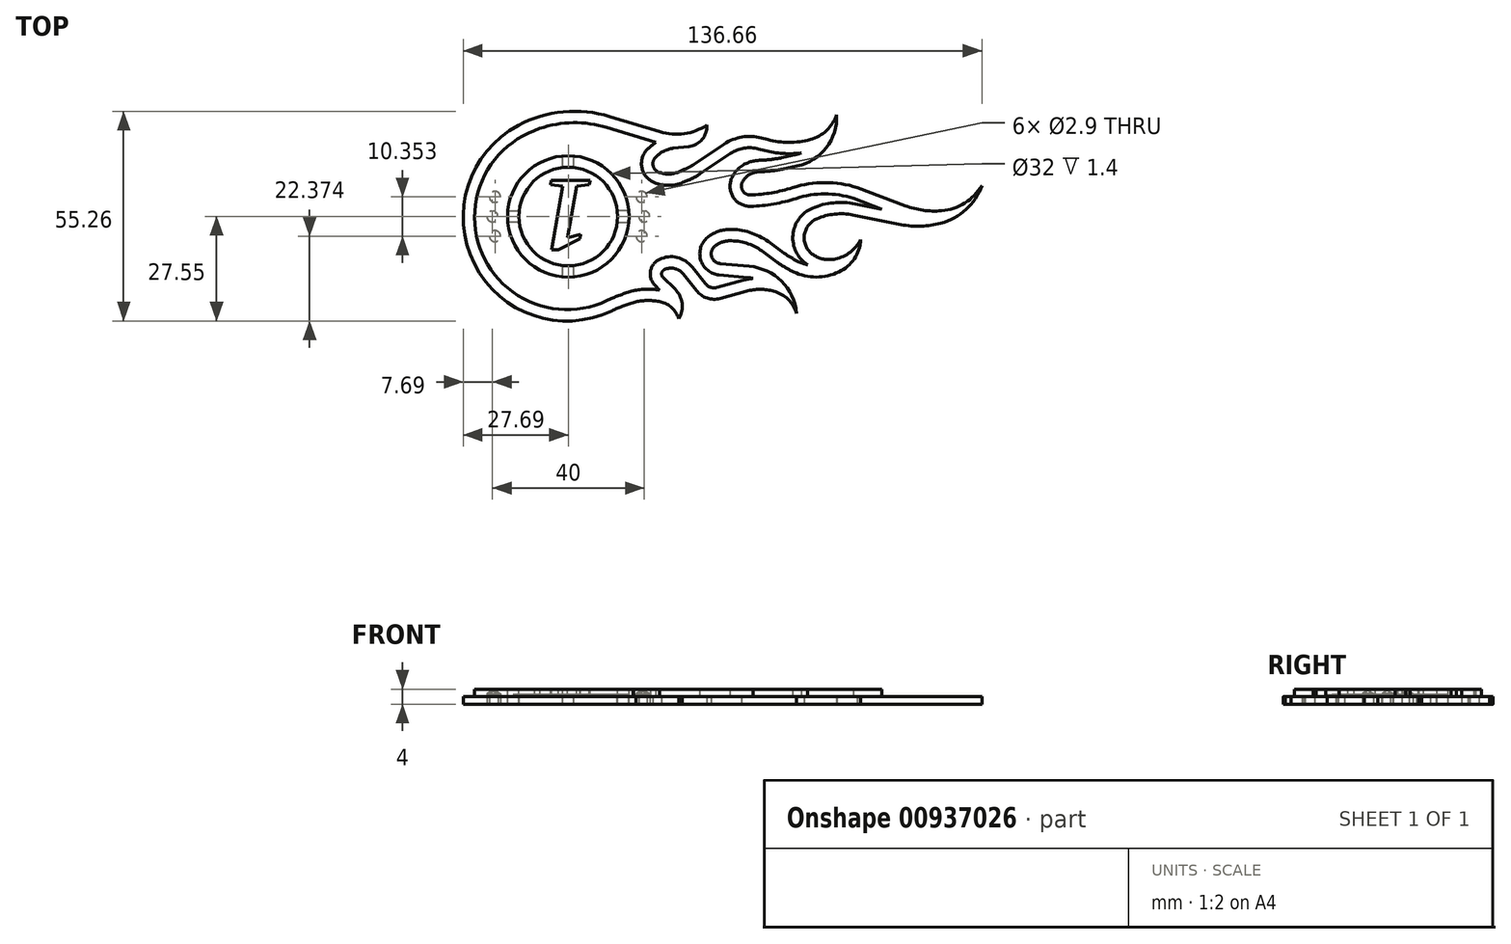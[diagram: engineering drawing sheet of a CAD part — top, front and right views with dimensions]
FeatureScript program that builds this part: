
annotation { "Feature Type Name" : "Feature", "Feature Type Description" : "" }
export const myFeature = defineFeature(function(context is Context, id is Id, definition is map)
    precondition{}
    {
        {
            var Q0;
            Q0=qCreatedBy(makeId("Top.planeOp"),FACE);
            var sketch = newSketch(context, id + "F0", { "sketchPlane" : qUnion([Q0])});
            skArc(sketch, "E0", {"start": v(-15.8, 20.8) * mm, "mid": v(-9.44, 20.3) * mm, "end": v(-3.49, 22.58) * mm});
            skLineSegment(sketch, "E1", {"start": v(-29, 24.82) * mm, "end": v(-15.8, 20.8) * mm});
            skArc(sketch, "E2", {"start": v(-53.14, 22.5) * mm, "mid": v(-64.76, -14.01) * mm, "end": v(-28.48, -26.36) * mm});
            skArc(sketch, "E3", {"start": v(-29, 24.82) * mm, "mid": v(-41.3, 26.06) * mm, "end": v(-53.14, 22.5) * mm});
            skArc(sketch, "E4", {"start": v(-8.25, 16.94) * mm, "mid": v(-4.75, 18.81) * mm, "end": v(-3.49, 22.58) * mm});
            skArc(sketch, "E5", {"start": v(-10.87, -28.44) * mm, "mid": v(-12.7, -25.58) * mm, "end": v(-15.7, -24) * mm});
            skArc(sketch, "E6", {"start": v(-15.7, -24) * mm, "mid": v(-18.94, -23.64) * mm, "end": v(-22.18, -24) * mm});
            skArc(sketch, "E7", {"start": v(-22.18, -24) * mm, "mid": v(-25.39, -25.04) * mm, "end": v(-28.48, -26.36) * mm});
            skArc(sketch, "E8", {"start": v(-10.87, -28.44) * mm, "mid": v(-10.04, -24.35) * mm, "end": v(-11.9, -20.62) * mm});
            skArc(sketch, "E9", {"start": v(-14.69, -15.51) * mm, "mid": v(-15.4, -16.45) * mm, "end": v(-15.02, -17.57) * mm});
            skLineSegment(sketch, "E10", {"start": v(-11.9, -20.62) * mm, "end": v(-15.02, -17.57) * mm});
            skArc(sketch, "E11", {"start": v(-9.7, -16.65) * mm, "mid": v(-12, -15.2) * mm, "end": v(-14.69, -15.51) * mm});
            skLineSegment(sketch, "E12", {"start": v(-9.7, -16.65) * mm, "end": v(-6.22, -21.05) * mm});
            skArc(sketch, "E13", {"start": v(-6.22, -21.05) * mm, "mid": v(-3.42, -23) * mm, "end": v(0, -23.09) * mm});
            skLineSegment(sketch, "E14", {"start": v(-8.25, 16.94) * mm, "end": v(-12.34, 16.47) * mm});
            skArc(sketch, "E15", {"start": v(-12.34, 16.47) * mm, "mid": v(-14.96, 15.66) * mm, "end": v(-17.12, 13.97) * mm});
            skArc(sketch, "E16", {"start": v(-17.12, 13.97) * mm, "mid": v(-17.66, 11.88) * mm, "end": v(-16.27, 10.22) * mm});
            skArc(sketch, "E17", {"start": v(-16.27, 10.22) * mm, "mid": v(-13.63, 9.69) * mm, "end": v(-10.98, 10.22) * mm});
            skLineSegment(sketch, "E18", {"start": v(-10.98, 10.22) * mm, "end": v(-9.42, 10.88) * mm});
            skLineSegment(sketch, "E19", {"start": v(1.1, 17.58) * mm, "end": v(-6.91, 12.23) * mm});
            skArc(sketch, "E20.filletArc", {"start": v(-9.42, 10.88) * mm, "mid": v(-8.13, 11.5) * mm, "end": v(-6.91, 12.23) * mm});
            skArc(sketch, "E21", {"start": v(10.9, 19.2) * mm, "mid": v(5.82, 19.45) * mm, "end": v(1.1, 17.58) * mm});
            skLineSegment(sketch, "E22", {"start": v(10.9, 19.2) * mm, "end": v(12.5, 18.78) * mm});
            skArc(sketch, "E23", {"start": v(12.5, 18.78) * mm, "mid": v(18.13, 18.04) * mm, "end": v(23.76, 18.78) * mm});
            skArc(sketch, "E24", {"start": v(23.76, 18.78) * mm, "mid": v(28.06, 21.17) * mm, "end": v(30.72, 25.31) * mm});
            skArc(sketch, "E25", {"start": v(20.3, 11.8) * mm, "mid": v(27.98, 16.65) * mm, "end": v(30.72, 25.31) * mm});
            skLineSegment(sketch, "E26", {"start": v(20.3, 11.8) * mm, "end": v(16.86, 11.06) * mm});
            skArc(sketch, "E27", {"start": v(10.82, 10.32) * mm, "mid": v(13.86, 10.55) * mm, "end": v(16.86, 11.06) * mm});
            skArc(sketch, "E28", {"start": v(10.82, 10.32) * mm, "mid": v(9.84, 10.23) * mm, "end": v(8.87, 10.03) * mm});
            skArc(sketch, "E29", {"start": v(8.87, 10.03) * mm, "mid": v(7.03, 9.04) * mm, "end": v(5.8, 7.34) * mm});
            skArc(sketch, "E30", {"start": v(5.8, 7.34) * mm, "mid": v(6.02, 5.16) * mm, "end": v(7.97, 4.17) * mm});
            skArc(sketch, "E31", {"start": v(19.12, 6.1) * mm, "mid": v(13.61, 4.74) * mm, "end": v(7.97, 4.17) * mm});
            skArc(sketch, "E32", {"start": v(36.14, 6.1) * mm, "mid": v(27.63, 7.44) * mm, "end": v(19.12, 6.1) * mm});
            skLineSegment(sketch, "E33", {"start": v(0, -23.09) * mm, "end": v(6.9, -21.19) * mm});
            skArc(sketch, "E34", {"start": v(14.19, -21.19) * mm, "mid": v(10.54, -20.7) * mm, "end": v(6.9, -21.19) * mm});
            skArc(sketch, "E35", {"start": v(20.17, -27.02) * mm, "mid": v(17.93, -23.33) * mm, "end": v(14.19, -21.19) * mm});
            skArc(sketch, "E36", {"start": v(20.17, -27.02) * mm, "mid": v(16.15, -18.57) * mm, "end": v(7.68, -14.62) * mm});
            skLineSegment(sketch, "E37", {"start": v(7.68, -14.62) * mm, "end": v(0, -13.91) * mm});
            skArc(sketch, "E38", {"start": v(-1.39, -9.32) * mm, "mid": v(-2.24, -12.08) * mm, "end": v(0, -13.91) * mm});
            skArc(sketch, "E39", {"start": v(2.46, -7.92) * mm, "mid": v(0.42, -8.3) * mm, "end": v(-1.39, -9.32) * mm});
            skArc(sketch, "E40", {"start": v(10.98, -10.59) * mm, "mid": v(6.94, -8.56) * mm, "end": v(2.46, -7.92) * mm});
            skLineSegment(sketch, "E41", {"start": v(10.98, -10.59) * mm, "end": v(15.06, -13.54) * mm});
            skArc(sketch, "E42", {"start": v(15.06, -13.54) * mm, "mid": v(17.16, -14.93) * mm, "end": v(19.37, -16.1) * mm});
            skArc(sketch, "E43", {"start": v(19.37, -16.1) * mm, "mid": v(25.34, -17.46) * mm, "end": v(31.3, -16.1) * mm});
            skArc(sketch, "E44", {"start": v(31.3, -16.1) * mm, "mid": v(35.34, -12.64) * mm, "end": v(37.05, -7.6) * mm});
            skArc(sketch, "E45", {"start": v(30.4, -12.7) * mm, "mid": v(34.29, -10.88) * mm, "end": v(37.05, -7.6) * mm});
            skArc(sketch, "E46", {"start": v(24.84, -11.81) * mm, "mid": v(27.53, -12.78) * mm, "end": v(30.4, -12.7) * mm});
            skArc(sketch, "E47", {"start": v(25.48, -2.1) * mm, "mid": v(22.17, -6.76) * mm, "end": v(24.84, -11.81) * mm});
            skArc(sketch, "E48", {"start": v(35.02, -1.1) * mm, "mid": v(30.17, -0.88) * mm, "end": v(25.48, -2.1) * mm});
            skLineSegment(sketch, "E49", {"start": v(35.02, -1.1) * mm, "end": v(47.7, -3.63) * mm});
            skArc(sketch, "E50", {"start": v(47.7, -3.63) * mm, "mid": v(52.94, -4.06) * mm, "end": v(58.13, -3.3) * mm});
            skArc(sketch, "E51", {"start": v(58.13, -3.3) * mm, "mid": v(64.79, 0.34) * mm, "end": v(68.97, 6.67) * mm});
            skArc(sketch, "E52", {"start": v(58.36, 0) * mm, "mid": v(64.48, 2.05) * mm, "end": v(68.97, 6.67) * mm});
            skArc(sketch, "E53", {"start": v(48.76, 1.34) * mm, "mid": v(53.49, 0.13) * mm, "end": v(58.36, 0) * mm});
            skLineSegment(sketch, "E54", {"start": v(36.14, 6.1) * mm, "end": v(48.76, 1.34) * mm});
            skArc(sketch, "E55.0", {"start": v(-12.68, 19.45) * mm, "mid": v(-12.7, 19.44) * mm, "end": v(-12.72, 19.44) * mm});
            skLineSegment(sketch, "E56", {"start": v(-16.92, 18) * mm, "end": v(-16.92, 18) * mm});
            skLineSegment(sketch, "E57", {"start": v(-19.37, 15.96) * mm, "end": v(-19.34, 15.99) * mm});
            skSolve(sketch);
        }
        {
            var Q0;
            Q0=qSketchRegion(id+"F0",true);
            extrude(context, id + "F1", {"entities" : qUnion([Q0]), "depth" : 2 * mm, "offsetDistance" : 25 * mm});
        }
        {
            var Q0;
            Q0=makeQuery(id+"F1.opExtrude","CAP_FACE",FACE,{"disambiguationData":[OSD([sQuery(id+"F0.wireOp",EDGE,"E0"),sQuery(id+"F0.wireOp",EDGE,"E1"),sQuery(id+"F0.wireOp",EDGE,"E2"),sQuery(id+"F0.wireOp",EDGE,"E3"),sQuery(id+"F0.wireOp",EDGE,"E4"),sQuery(id+"F0.wireOp",EDGE,"E5"),sQuery(id+"F0.wireOp",EDGE,"E6"),sQuery(id+"F0.wireOp",EDGE,"E7"),sQuery(id+"F0.wireOp",EDGE,"E8"),sQuery(id+"F0.wireOp",EDGE,"E9"),sQuery(id+"F0.wireOp",EDGE,"E10"),sQuery(id+"F0.wireOp",EDGE,"E11"),sQuery(id+"F0.wireOp",EDGE,"E12"),sQuery(id+"F0.wireOp",EDGE,"E13"),sQuery(id+"F0.wireOp",EDGE,"E14"),sQuery(id+"F0.wireOp",EDGE,"E15"),sQuery(id+"F0.wireOp",EDGE,"E16"),sQuery(id+"F0.wireOp",EDGE,"E17"),sQuery(id+"F0.wireOp",EDGE,"E18"),sQuery(id+"F0.wireOp",EDGE,"E19"),sQuery(id+"F0.wireOp",EDGE,"E20.filletArc"),sQuery(id+"F0.wireOp",EDGE,"E21"),sQuery(id+"F0.wireOp",EDGE,"E22"),sQuery(id+"F0.wireOp",EDGE,"E23"),sQuery(id+"F0.wireOp",EDGE,"E24"),sQuery(id+"F0.wireOp",EDGE,"E25"),sQuery(id+"F0.wireOp",EDGE,"E26"),sQuery(id+"F0.wireOp",EDGE,"E27"),sQuery(id+"F0.wireOp",EDGE,"E28"),sQuery(id+"F0.wireOp",EDGE,"E29"),sQuery(id+"F0.wireOp",EDGE,"E30"),sQuery(id+"F0.wireOp",EDGE,"E31"),sQuery(id+"F0.wireOp",EDGE,"E32"),sQuery(id+"F0.wireOp",EDGE,"E33"),sQuery(id+"F0.wireOp",EDGE,"E34"),sQuery(id+"F0.wireOp",EDGE,"E35"),sQuery(id+"F0.wireOp",EDGE,"E36"),sQuery(id+"F0.wireOp",EDGE,"E37"),sQuery(id+"F0.wireOp",EDGE,"E38"),sQuery(id+"F0.wireOp",EDGE,"E39"),sQuery(id+"F0.wireOp",EDGE,"E40"),sQuery(id+"F0.wireOp",EDGE,"E41"),sQuery(id+"F0.wireOp",EDGE,"E42"),sQuery(id+"F0.wireOp",EDGE,"E43"),sQuery(id+"F0.wireOp",EDGE,"E44"),sQuery(id+"F0.wireOp",EDGE,"E45"),sQuery(id+"F0.wireOp",EDGE,"E46"),sQuery(id+"F0.wireOp",EDGE,"E47"),sQuery(id+"F0.wireOp",EDGE,"E48"),sQuery(id+"F0.wireOp",EDGE,"E49"),sQuery(id+"F0.wireOp",EDGE,"E50"),sQuery(id+"F0.wireOp",EDGE,"E51"),sQuery(id+"F0.wireOp",EDGE,"E52"),sQuery(id+"F0.wireOp",EDGE,"E53"),sQuery(id+"F0.wireOp",EDGE,"E54")])],"isStart":false});
            var sketch = newSketch(context, id + "F2", { "sketchPlane" : qUnion([Q0])});
            skArc(sketch, "E58", {"start": v(-24.07, -3) * mm, "mid": v(-24, -1.5) * mm, "end": v(-24.07, 0) * mm});
            skArc(sketch, "E59", {"start": v(-27.09, -3) * mm, "mid": v(-27, -1.5) * mm, "end": v(-27.09, 0) * mm});
            skArc(sketch, "E60", {"start": v(-38.5, 11.41) * mm, "mid": v(-40, 11.5) * mm, "end": v(-41.5, 11.41) * mm});
            skArc(sketch, "E61", {"start": v(-38.5, 14.43) * mm, "mid": v(-40, 14.5) * mm, "end": v(-41.5, 14.43) * mm});
            skArc(sketch, "E62", {"start": v(-41.5, -14.41) * mm, "mid": v(-40, -14.5) * mm, "end": v(-38.5, -14.41) * mm});
            skArc(sketch, "E63", {"start": v(-41.5, -17.43) * mm, "mid": v(-40, -17.5) * mm, "end": v(-38.5, -17.43) * mm});
            skArc(sketch, "E64", {"start": v(-55.93, 0) * mm, "mid": v(-56, -1.5) * mm, "end": v(-55.93, -3) * mm});
            skArc(sketch, "E65", {"start": v(-52.91, 0.02) * mm, "mid": v(-53, -1.5) * mm, "end": v(-52.91, -3) * mm});
            skLineSegment(sketch, "E66", {"start": v(-41.5, -17.43) * mm, "end": v(-41.5, -14.41) * mm});
            skLineSegment(sketch, "E67", {"start": v(-38.5, -17.43) * mm, "end": v(-38.5, -14.41) * mm});
            skLineSegment(sketch, "E68", {"start": v(-27.09, -3) * mm, "end": v(-24.07, -3) * mm});
            skLineSegment(sketch, "E69", {"start": v(-24.07, 0) * mm, "end": v(-27.09, 0) * mm});
            skLineSegment(sketch, "E70", {"start": v(-38.5, 11.41) * mm, "end": v(-38.5, 14.43) * mm});
            skLineSegment(sketch, "E71", {"start": v(-41.5, 11.41) * mm, "end": v(-41.5, 14.43) * mm});
            skLineSegment(sketch, "E72", {"start": v(-52.91, -3) * mm, "end": v(-55.93, -3) * mm});
            skLineSegment(sketch, "E73", {"start": v(-55.93, 0) * mm, "end": v(-52.91, 0.02) * mm});
            skSolve(sketch);
        }
        {
            var Q0;
            Q0=makeQuery(id+"F1.opExtrude","CAP_FACE",FACE,{"disambiguationData":[OSD([sQuery(id+"F0.wireOp",EDGE,"E0"),sQuery(id+"F0.wireOp",EDGE,"E1"),sQuery(id+"F0.wireOp",EDGE,"E2"),sQuery(id+"F0.wireOp",EDGE,"E3"),sQuery(id+"F0.wireOp",EDGE,"E4"),sQuery(id+"F0.wireOp",EDGE,"E5"),sQuery(id+"F0.wireOp",EDGE,"E6"),sQuery(id+"F0.wireOp",EDGE,"E7"),sQuery(id+"F0.wireOp",EDGE,"E8"),sQuery(id+"F0.wireOp",EDGE,"E9"),sQuery(id+"F0.wireOp",EDGE,"E10"),sQuery(id+"F0.wireOp",EDGE,"E11"),sQuery(id+"F0.wireOp",EDGE,"E12"),sQuery(id+"F0.wireOp",EDGE,"E13"),sQuery(id+"F0.wireOp",EDGE,"E14"),sQuery(id+"F0.wireOp",EDGE,"E15"),sQuery(id+"F0.wireOp",EDGE,"E16"),sQuery(id+"F0.wireOp",EDGE,"E17"),sQuery(id+"F0.wireOp",EDGE,"E18"),sQuery(id+"F0.wireOp",EDGE,"E19"),sQuery(id+"F0.wireOp",EDGE,"E20.filletArc"),sQuery(id+"F0.wireOp",EDGE,"E21"),sQuery(id+"F0.wireOp",EDGE,"E22"),sQuery(id+"F0.wireOp",EDGE,"E23"),sQuery(id+"F0.wireOp",EDGE,"E24"),sQuery(id+"F0.wireOp",EDGE,"E25"),sQuery(id+"F0.wireOp",EDGE,"E26"),sQuery(id+"F0.wireOp",EDGE,"E27"),sQuery(id+"F0.wireOp",EDGE,"E28"),sQuery(id+"F0.wireOp",EDGE,"E29"),sQuery(id+"F0.wireOp",EDGE,"E30"),sQuery(id+"F0.wireOp",EDGE,"E31"),sQuery(id+"F0.wireOp",EDGE,"E32"),sQuery(id+"F0.wireOp",EDGE,"E33"),sQuery(id+"F0.wireOp",EDGE,"E34"),sQuery(id+"F0.wireOp",EDGE,"E35"),sQuery(id+"F0.wireOp",EDGE,"E36"),sQuery(id+"F0.wireOp",EDGE,"E37"),sQuery(id+"F0.wireOp",EDGE,"E38"),sQuery(id+"F0.wireOp",EDGE,"E39"),sQuery(id+"F0.wireOp",EDGE,"E40"),sQuery(id+"F0.wireOp",EDGE,"E41"),sQuery(id+"F0.wireOp",EDGE,"E42"),sQuery(id+"F0.wireOp",EDGE,"E43"),sQuery(id+"F0.wireOp",EDGE,"E44"),sQuery(id+"F0.wireOp",EDGE,"E45"),sQuery(id+"F0.wireOp",EDGE,"E46"),sQuery(id+"F0.wireOp",EDGE,"E47"),sQuery(id+"F0.wireOp",EDGE,"E48"),sQuery(id+"F0.wireOp",EDGE,"E49"),sQuery(id+"F0.wireOp",EDGE,"E50"),sQuery(id+"F0.wireOp",EDGE,"E51"),sQuery(id+"F0.wireOp",EDGE,"E52"),sQuery(id+"F0.wireOp",EDGE,"E53"),sQuery(id+"F0.wireOp",EDGE,"E54")])],"isStart":false});
            var sketch = newSketch(context, id + "F3", { "sketchPlane" : qUnion([Q0])});
            skArc(sketch, "E74.0", {"start": v(-29.87, 21.95) * mm, "mid": v(-38.73, 23.2) * mm, "end": v(-47.54, 21.67) * mm});
            skArc(sketch, "E75", {"start": v(-48.94, 21.12) * mm, "mid": v(-62.73, -11.25) * mm, "end": v(-29.8, -23.67) * mm});
            skLineSegment(sketch, "E76", {"start": v(-48.94, 21.12) * mm, "end": v(-47.54, 21.67) * mm});
            skLineSegment(sketch, "E77.0", {"start": v(-29.87, 21.95) * mm, "end": v(-16.92, 18) * mm});
            skLineSegment(sketch, "E78", {"start": v(-20.59, 18.76) * mm, "end": v(-20.59, 18.76) * mm});
            skArc(sketch, "E79", {"start": v(-16.92, 18) * mm, "mid": v(-18.2, 17.08) * mm, "end": v(-19.34, 15.99) * mm});
            skArc(sketch, "E80.0", {"start": v(-19.37, 15.96) * mm, "mid": v(-20.58, 11.21) * mm, "end": v(-17.43, 7.46) * mm});
            skArc(sketch, "E81.0", {"start": v(-17.43, 7.46) * mm, "mid": v(-13.63, 6.69) * mm, "end": v(-9.82, 7.46) * mm});
            skLineSegment(sketch, "E82.0", {"start": v(-9.82, 7.46) * mm, "end": v(-8.25, 8.12) * mm});
            skArc(sketch, "E83.0", {"start": v(-8.25, 8.12) * mm, "mid": v(-6.71, 8.86) * mm, "end": v(-5.25, 9.74) * mm});
            skLineSegment(sketch, "E84.0", {"start": v(2.76, 15.09) * mm, "end": v(-5.25, 9.74) * mm});
            skArc(sketch, "E85.0", {"start": v(10.13, 16.3) * mm, "mid": v(6.31, 16.5) * mm, "end": v(2.76, 15.09) * mm});
            skLineSegment(sketch, "E86.0", {"start": v(10.13, 16.3) * mm, "end": v(11.74, 15.88) * mm});
            skArc(sketch, "E87.0", {"start": v(11.74, 15.88) * mm, "mid": v(16.51, 15.1) * mm, "end": v(21.35, 15.25) * mm});
            skLineSegment(sketch, "E88.0", {"start": v(19.3, 14.65) * mm, "end": v(16.22, 13.99) * mm});
            skArc(sketch, "E89.0", {"start": v(19.66, 14.73) * mm, "mid": v(20.52, 14.95) * mm, "end": v(21.35, 15.25) * mm});
            skArc(sketch, "E90.0", {"start": v(10.73, 13.32) * mm, "mid": v(13.5, 13.53) * mm, "end": v(16.22, 13.99) * mm});
            skArc(sketch, "E91.0", {"start": v(10.73, 13.32) * mm, "mid": v(9.4, 13.2) * mm, "end": v(8.08, 12.92) * mm});
            skArc(sketch, "E92.0", {"start": v(8.08, 12.92) * mm, "mid": v(5.05, 11.3) * mm, "end": v(3.04, 8.52) * mm});
            skArc(sketch, "E93.0", {"start": v(3.04, 8.52) * mm, "mid": v(3.54, 3.47) * mm, "end": v(8.07, 1.17) * mm});
            skArc(sketch, "E94.0", {"start": v(20.04, 3.24) * mm, "mid": v(14.12, 1.79) * mm, "end": v(8.07, 1.17) * mm});
            skLineSegment(sketch, "E95.0", {"start": v(35.6, 1.84) * mm, "end": v(42.66, 0.43) * mm});
            skArc(sketch, "E96.0", {"start": v(35.6, 1.84) * mm, "mid": v(29.87, 2.1) * mm, "end": v(24.3, 0.67) * mm});
            skArc(sketch, "E97.0", {"start": v(24.3, 0.67) * mm, "mid": v(19.19, -6.38) * mm, "end": v(23, -14.2) * mm});
            skArc(sketch, "E98.0", {"start": v(20.66, -13.4) * mm, "mid": v(21.81, -13.87) * mm, "end": v(23, -14.2) * mm});
            skArc(sketch, "E99.0", {"start": v(16.82, -11.12) * mm, "mid": v(18.69, -12.35) * mm, "end": v(20.66, -13.4) * mm});
            skLineSegment(sketch, "E100.0", {"start": v(12.74, -8.16) * mm, "end": v(16.82, -11.12) * mm});
            skArc(sketch, "E101.0", {"start": v(12.74, -8.16) * mm, "mid": v(7.83, -5.7) * mm, "end": v(2.4, -4.92) * mm});
            skArc(sketch, "E102.0", {"start": v(2.4, -4.92) * mm, "mid": v(-0.61, -5.48) * mm, "end": v(-3.27, -7) * mm});
            skArc(sketch, "E103.0", {"start": v(-3.27, -7) * mm, "mid": v(-5.11, -12.95) * mm, "end": v(-0.27, -16.9) * mm});
            skLineSegment(sketch, "E104.0", {"start": v(7.4, -17.6) * mm, "end": v(-0.27, -16.9) * mm});
            skLineSegment(sketch, "E105.0", {"start": v(-0.8, -20.2) * mm, "end": v(6.1, -18.3) * mm});
            skArc(sketch, "E106", {"start": v(8.67, -17.8) * mm, "mid": v(8.04, -17.68) * mm, "end": v(7.4, -17.6) * mm});
            skArc(sketch, "E107", {"start": v(8.67, -17.8) * mm, "mid": v(7.38, -18) * mm, "end": v(6.1, -18.3) * mm});
            skArc(sketch, "E108.0", {"start": v(-3.87, -19.2) * mm, "mid": v(-2.48, -20.16) * mm, "end": v(-0.8, -20.2) * mm});
            skLineSegment(sketch, "E109.0", {"start": v(-7.35, -14.8) * mm, "end": v(-3.87, -19.2) * mm});
            skArc(sketch, "E110.0", {"start": v(-7.35, -14.8) * mm, "mid": v(-11.32, -12.28) * mm, "end": v(-16, -12.81) * mm});
            skArc(sketch, "E111.0", {"start": v(-16, -12.81) * mm, "mid": v(-18.35, -15.97) * mm, "end": v(-17.12, -19.72) * mm});
            skLineSegment(sketch, "E112.0", {"start": v(-15.9, -20.9) * mm, "end": v(-17.12, -19.72) * mm});
            skArc(sketch, "E113.0", {"start": v(-15.9, -20.9) * mm, "mid": v(-19.4, -20.64) * mm, "end": v(-22.85, -21.08) * mm});
            skArc(sketch, "E114.0", {"start": v(-22.98, -21.11) * mm, "mid": v(-26.29, -22.18) * mm, "end": v(-29.49, -23.52) * mm});
            skLineSegment(sketch, "E115", {"start": v(-22.98, -21.11) * mm, "end": v(-22.85, -21.08) * mm});
            skLineSegment(sketch, "E116", {"start": v(19.3, 14.65) * mm, "end": v(19.66, 14.73) * mm});
            skLineSegment(sketch, "E117", {"start": v(-19.37, 15.96) * mm, "end": v(-19.34, 15.99) * mm});
            skArc(sketch, "E118", {"start": v(35.15, 3.27) * mm, "mid": v(27.6, 4.44) * mm, "end": v(20.04, 3.24) * mm});
            skLineSegment(sketch, "E119", {"start": v(35.15, 3.27) * mm, "end": v(42.66, 0.43) * mm});
            skLineSegment(sketch, "E120", {"start": v(-29.8, -23.67) * mm, "end": v(-29.49, -23.52) * mm});
            skSolve(sketch);
        }
        {
            var Q0;
            Q0=qSketchRegion(id+"F2",true);
            extrude(context, id + "F4", {"entities" : qUnion([Q0]), "operationType" : NewBodyOperationType.REMOVE, "oppositeDirection" : true, "depth" : 2 * mm, "offsetDistance" : 25 * mm});
        }
        {
            var Q0;
            Q0=qSketchRegion(id+"F3",true);
            extrude(context, id + "F5", {"entities" : qUnion([Q0]), "operationType" : NewBodyOperationType.ADD, "depth" : 2 * mm, "offsetDistance" : 25 * mm});
        }
        {
            var Q0;
            Q0=makeQuery(id+"F5.opExtrude","CAP_FACE",FACE,{"disambiguationData":[OSD([sQuery(id+"F3.wireOp",EDGE,"E74.0"),sQuery(id+"F3.wireOp",EDGE,"E75"),sQuery(id+"F3.wireOp",EDGE,"E76"),sQuery(id+"F3.wireOp",EDGE,"E77.0"),sQuery(id+"F3.wireOp",EDGE,"E79"),sQuery(id+"F3.wireOp",EDGE,"E80.0"),sQuery(id+"F3.wireOp",EDGE,"E81.0"),sQuery(id+"F3.wireOp",EDGE,"E82.0"),sQuery(id+"F3.wireOp",EDGE,"E83.0"),sQuery(id+"F3.wireOp",EDGE,"E84.0"),sQuery(id+"F3.wireOp",EDGE,"E85.0"),sQuery(id+"F3.wireOp",EDGE,"E86.0"),sQuery(id+"F3.wireOp",EDGE,"E87.0"),sQuery(id+"F3.wireOp",EDGE,"E88.0"),sQuery(id+"F3.wireOp",EDGE,"E89.0"),sQuery(id+"F3.wireOp",EDGE,"E90.0"),sQuery(id+"F3.wireOp",EDGE,"E91.0"),sQuery(id+"F3.wireOp",EDGE,"E92.0"),sQuery(id+"F3.wireOp",EDGE,"E93.0"),sQuery(id+"F3.wireOp",EDGE,"E94.0"),sQuery(id+"F3.wireOp",EDGE,"E95.0"),sQuery(id+"F3.wireOp",EDGE,"E96.0"),sQuery(id+"F3.wireOp",EDGE,"E97.0"),sQuery(id+"F3.wireOp",EDGE,"E98.0"),sQuery(id+"F3.wireOp",EDGE,"E99.0"),sQuery(id+"F3.wireOp",EDGE,"E100.0"),sQuery(id+"F3.wireOp",EDGE,"E101.0"),sQuery(id+"F3.wireOp",EDGE,"E102.0"),sQuery(id+"F3.wireOp",EDGE,"E103.0"),sQuery(id+"F3.wireOp",EDGE,"E104.0"),sQuery(id+"F3.wireOp",EDGE,"E105.0"),sQuery(id+"F3.wireOp",EDGE,"E106"),sQuery(id+"F3.wireOp",EDGE,"E107"),sQuery(id+"F3.wireOp",EDGE,"E108.0"),sQuery(id+"F3.wireOp",EDGE,"E109.0"),sQuery(id+"F3.wireOp",EDGE,"E110.0"),sQuery(id+"F3.wireOp",EDGE,"E111.0"),sQuery(id+"F3.wireOp",EDGE,"E112.0"),sQuery(id+"F3.wireOp",EDGE,"E113.0"),sQuery(id+"F3.wireOp",EDGE,"E114.0"),sQuery(id+"F3.wireOp",EDGE,"E115"),sQuery(id+"F3.wireOp",EDGE,"E116"),sQuery(id+"F3.wireOp",EDGE,"E117"),sQuery(id+"F3.wireOp",EDGE,"E118"),sQuery(id+"F3.wireOp",EDGE,"E119"),sQuery(id+"F3.wireOp",EDGE,"E120")])],"isStart":false});
            var sketch = newSketch(context, id + "F6", { "sketchPlane" : qUnion([Q0])});
            skCircle(sketch, "E121", {"center": v(-40, -1.5) * mm, "radius": 16 * mm});
            skCircle(sketch, "E122", {"center": v(-40, -1.5) * mm, "radius": 13 * mm});
            skSolve(sketch);
        }
        {
            var Q0;
            Q0=qSketchRegion(id+"F6",true);
            extrude(context, id + "F7", {"entities" : qUnion([Q0]), "operationType" : NewBodyOperationType.REMOVE, "oppositeDirection" : true, "depth" : 1.4 * mm, "offsetDistance" : 25 * mm});
        }
        {
            var Q0;
            Q0=makeQuery(id+"F6.imprint","IMPRINT",FACE,{"disambiguationData":[TD([[makeQuery(id+"F6.imprint","IMPRINT",EDGE,{"derivedFrom":sQuery(id+"F6.wireOp",EDGE,"E121")}),-1.0]])]});
            var sketch = newSketch(context, id + "F8", { "sketchPlane" : qUnion([Q0])});
            skText(sketch, "E123", { "text": "1", "fontName": "Tinos-BoldItalic.ttf"});
            const initialGuessF8  = {"E123": [-0.0336, 0.008, -1, 0, 0.02]};
            skSetInitialGuess(sketch, initialGuessF8);
            skSolve(sketch);
        }
        {
            var Q0;
            Q0=qSketchRegion(id+"F8",true);
            extrude(context, id + "F9", {"entities" : qUnion([Q0]), "operationType" : NewBodyOperationType.REMOVE, "oppositeDirection" : true, "depth" : 1.4 * mm, "offsetDistance" : 25 * mm});
        }
        {
            var Q0;
            Q0=makeQuery(id+"F1.opExtrude","CAP_FACE",FACE,{"disambiguationData":[OSD([sQuery(id+"F0.wireOp",EDGE,"E0"),sQuery(id+"F0.wireOp",EDGE,"E1"),sQuery(id+"F0.wireOp",EDGE,"E2"),sQuery(id+"F0.wireOp",EDGE,"E3"),sQuery(id+"F0.wireOp",EDGE,"E4"),sQuery(id+"F0.wireOp",EDGE,"E5"),sQuery(id+"F0.wireOp",EDGE,"E6"),sQuery(id+"F0.wireOp",EDGE,"E7"),sQuery(id+"F0.wireOp",EDGE,"E8"),sQuery(id+"F0.wireOp",EDGE,"E9"),sQuery(id+"F0.wireOp",EDGE,"E10"),sQuery(id+"F0.wireOp",EDGE,"E11"),sQuery(id+"F0.wireOp",EDGE,"E12"),sQuery(id+"F0.wireOp",EDGE,"E13"),sQuery(id+"F0.wireOp",EDGE,"E14"),sQuery(id+"F0.wireOp",EDGE,"E15"),sQuery(id+"F0.wireOp",EDGE,"E16"),sQuery(id+"F0.wireOp",EDGE,"E17"),sQuery(id+"F0.wireOp",EDGE,"E18"),sQuery(id+"F0.wireOp",EDGE,"E19"),sQuery(id+"F0.wireOp",EDGE,"E20.filletArc"),sQuery(id+"F0.wireOp",EDGE,"E21"),sQuery(id+"F0.wireOp",EDGE,"E22"),sQuery(id+"F0.wireOp",EDGE,"E23"),sQuery(id+"F0.wireOp",EDGE,"E24"),sQuery(id+"F0.wireOp",EDGE,"E25"),sQuery(id+"F0.wireOp",EDGE,"E26"),sQuery(id+"F0.wireOp",EDGE,"E27"),sQuery(id+"F0.wireOp",EDGE,"E28"),sQuery(id+"F0.wireOp",EDGE,"E29"),sQuery(id+"F0.wireOp",EDGE,"E30"),sQuery(id+"F0.wireOp",EDGE,"E31"),sQuery(id+"F0.wireOp",EDGE,"E32"),sQuery(id+"F0.wireOp",EDGE,"E33"),sQuery(id+"F0.wireOp",EDGE,"E34"),sQuery(id+"F0.wireOp",EDGE,"E35"),sQuery(id+"F0.wireOp",EDGE,"E36"),sQuery(id+"F0.wireOp",EDGE,"E37"),sQuery(id+"F0.wireOp",EDGE,"E38"),sQuery(id+"F0.wireOp",EDGE,"E39"),sQuery(id+"F0.wireOp",EDGE,"E40"),sQuery(id+"F0.wireOp",EDGE,"E41"),sQuery(id+"F0.wireOp",EDGE,"E42"),sQuery(id+"F0.wireOp",EDGE,"E43"),sQuery(id+"F0.wireOp",EDGE,"E44"),sQuery(id+"F0.wireOp",EDGE,"E45"),sQuery(id+"F0.wireOp",EDGE,"E46"),sQuery(id+"F0.wireOp",EDGE,"E47"),sQuery(id+"F0.wireOp",EDGE,"E48"),sQuery(id+"F0.wireOp",EDGE,"E49"),sQuery(id+"F0.wireOp",EDGE,"E50"),sQuery(id+"F0.wireOp",EDGE,"E51"),sQuery(id+"F0.wireOp",EDGE,"E52"),sQuery(id+"F0.wireOp",EDGE,"E53"),sQuery(id+"F0.wireOp",EDGE,"E54")])],"isStart":true});
            var sketch = newSketch(context, id + "F10", { "sketchPlane" : qUnion([Q0])});
            skPoint(sketch, "E124", {"position": v(-60, 1.5) * mm});
            skPoint(sketch, "E125", {"position": v(-20, 1.5) * mm});
            skLineSegment(sketch, "E126", {"start": v(-59.32, 6.68) * mm, "end": v(-20.68, -3.68) * mm});
            skPoint(sketch, "E127.orphan", {"position": v(-40, 1.5) * mm});
            skCircle(sketch, "E128", {"center": v(-40, 1.5) * mm, "radius": 20 * mm});
            skLineSegment(sketch, "E129", {"start": v(-59.32, -3.68) * mm, "end": v(-20.68, 6.68) * mm});
            skPoint(sketch, "E130", {"position": v(-59.32, 6.68) * mm});
            skPoint(sketch, "E131", {"position": v(-59.32, -3.68) * mm});
            skPoint(sketch, "E132", {"position": v(-20.68, 6.68) * mm});
            skPoint(sketch, "E133", {"position": v(-20.68, -3.68) * mm});
            skSolve(sketch);
        }
        {
            var Q0;
            Q0=sQuery(id+"F10.wireOp",VERTEX,"E124");
            var Q1;
            Q1=sQuery(id+"F10.wireOp",VERTEX,"E125");
            var Q2;
            Q2=sQuery(id+"F10.wireOp",VERTEX,"E130");
            var Q3;
            Q3=sQuery(id+"F10.wireOp",VERTEX,"E131");
            var Q4;
            Q4=sQuery(id+"F10.wireOp",VERTEX,"E132");
            var Q5;
            Q5=sQuery(id+"F10.wireOp",VERTEX,"E133");
            var Q6;
            Q6=makeQuery(id+"F1.opExtrude","SWEPT_BODY",BODY,{"disambiguationData":[OSD([sQuery(id+"F0.wireOp",EDGE,"E0"),sQuery(id+"F0.wireOp",EDGE,"E1"),sQuery(id+"F0.wireOp",EDGE,"E2"),sQuery(id+"F0.wireOp",EDGE,"E3"),sQuery(id+"F0.wireOp",EDGE,"E4"),sQuery(id+"F0.wireOp",EDGE,"E5"),sQuery(id+"F0.wireOp",EDGE,"E6"),sQuery(id+"F0.wireOp",EDGE,"E7"),sQuery(id+"F0.wireOp",EDGE,"E8"),sQuery(id+"F0.wireOp",EDGE,"E9"),sQuery(id+"F0.wireOp",EDGE,"E10"),sQuery(id+"F0.wireOp",EDGE,"E11"),sQuery(id+"F0.wireOp",EDGE,"E12"),sQuery(id+"F0.wireOp",EDGE,"E13"),sQuery(id+"F0.wireOp",EDGE,"E14"),sQuery(id+"F0.wireOp",EDGE,"E15"),sQuery(id+"F0.wireOp",EDGE,"E16"),sQuery(id+"F0.wireOp",EDGE,"E17"),sQuery(id+"F0.wireOp",EDGE,"E18"),sQuery(id+"F0.wireOp",EDGE,"E19"),sQuery(id+"F0.wireOp",EDGE,"E20.filletArc"),sQuery(id+"F0.wireOp",EDGE,"E21"),sQuery(id+"F0.wireOp",EDGE,"E22"),sQuery(id+"F0.wireOp",EDGE,"E23"),sQuery(id+"F0.wireOp",EDGE,"E24"),sQuery(id+"F0.wireOp",EDGE,"E25"),sQuery(id+"F0.wireOp",EDGE,"E26"),sQuery(id+"F0.wireOp",EDGE,"E27"),sQuery(id+"F0.wireOp",EDGE,"E28"),sQuery(id+"F0.wireOp",EDGE,"E29"),sQuery(id+"F0.wireOp",EDGE,"E30"),sQuery(id+"F0.wireOp",EDGE,"E31"),sQuery(id+"F0.wireOp",EDGE,"E32"),sQuery(id+"F0.wireOp",EDGE,"E33"),sQuery(id+"F0.wireOp",EDGE,"E34"),sQuery(id+"F0.wireOp",EDGE,"E35"),sQuery(id+"F0.wireOp",EDGE,"E36"),sQuery(id+"F0.wireOp",EDGE,"E37"),sQuery(id+"F0.wireOp",EDGE,"E38"),sQuery(id+"F0.wireOp",EDGE,"E39"),sQuery(id+"F0.wireOp",EDGE,"E40"),sQuery(id+"F0.wireOp",EDGE,"E41"),sQuery(id+"F0.wireOp",EDGE,"E42"),sQuery(id+"F0.wireOp",EDGE,"E43"),sQuery(id+"F0.wireOp",EDGE,"E44"),sQuery(id+"F0.wireOp",EDGE,"E45"),sQuery(id+"F0.wireOp",EDGE,"E46"),sQuery(id+"F0.wireOp",EDGE,"E47"),sQuery(id+"F0.wireOp",EDGE,"E48"),sQuery(id+"F0.wireOp",EDGE,"E49"),sQuery(id+"F0.wireOp",EDGE,"E50"),sQuery(id+"F0.wireOp",EDGE,"E51"),sQuery(id+"F0.wireOp",EDGE,"E52"),sQuery(id+"F0.wireOp",EDGE,"E53"),sQuery(id+"F0.wireOp",EDGE,"E54")])]});
            hole(context, id + "F11", {"style" : HoleStyle.SIMPLE, "endStyle" : HoleEndStyle.BLIND, "holeDiameter" : 2.9 * mm, "majorDiameter" : 5 * mm, "holeDepth" : 2.8 * mm, "isTappedThrough" : true, "tappedDepth" : 12 * mm, "tapClearance" : 3, "startFromSketch" : true, "locations" : qUnion([Q0, Q1, Q2, Q3, Q4, Q5]), "scope" : qUnion([Q6])});
        }
    });
